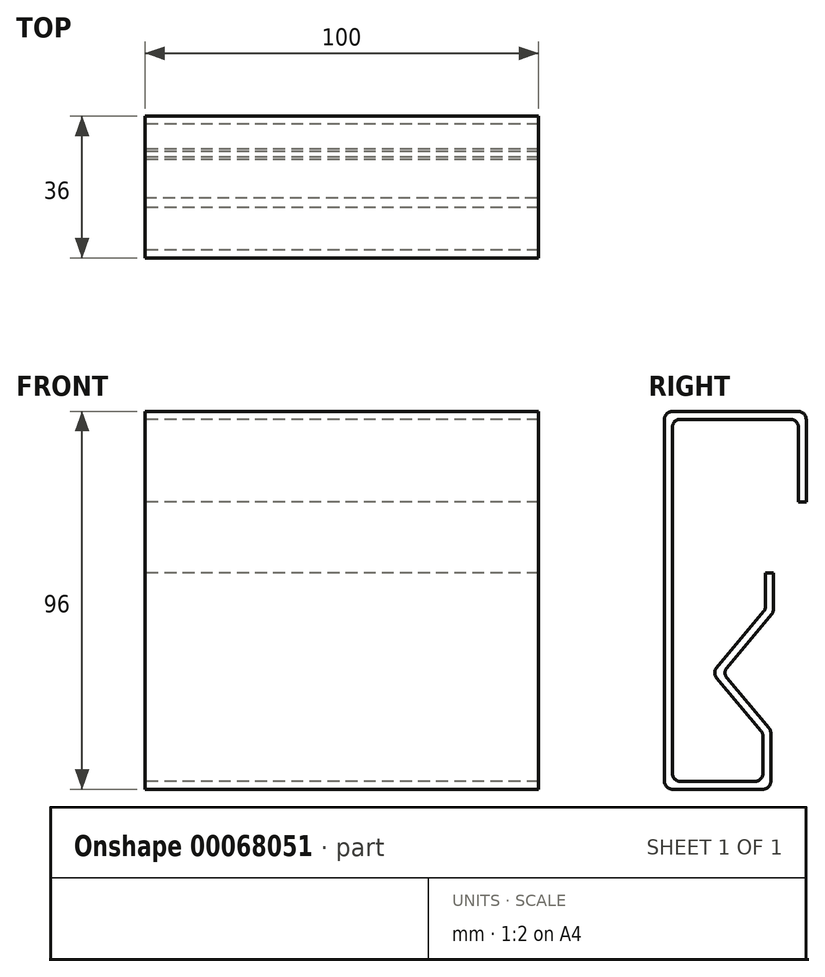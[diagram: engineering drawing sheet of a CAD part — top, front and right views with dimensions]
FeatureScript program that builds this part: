
annotation { "Feature Type Name" : "Feature", "Feature Type Description" : "" }
export const myFeature = defineFeature(function(context is Context, id is Id, definition is map)
    precondition{}
    {
        {
            var Q0;
            Q0=qCreatedBy(makeId("Right.planeOp"),FACE);
            var sketch = newSketch(context, id + "F0", { "sketchPlane" : qUnion([Q0])});
            skLineSegment(sketch, "E0", {"start": v(36, -23) * mm, "end": v(36, 0) * mm});
            skLineSegment(sketch, "E1", {"start": v(36, 0) * mm, "end": v(0, 0) * mm});
            skLineSegment(sketch, "E2", {"start": v(0, 0) * mm, "end": v(0, -96) * mm});
            skLineSegment(sketch, "E3", {"start": v(0, -96) * mm, "end": v(27, -96) * mm});
            skLineSegment(sketch, "E4", {"start": v(34, -23) * mm, "end": v(36, -23) * mm});
            skLineSegment(sketch, "E5.1", {"start": v(2, -2) * mm, "end": v(2, -94) * mm});
            skLineSegment(sketch, "E5.2", {"start": v(34, -2) * mm, "end": v(2, -2) * mm});
            skLineSegment(sketch, "E5.3", {"start": v(34, -23) * mm, "end": v(34, -2) * mm});
            skLineSegment(sketch, "E6", {"start": v(27, -96) * mm, "end": v(27, -81) * mm});
            skLineSegment(sketch, "E7", {"start": v(27, -81) * mm, "end": v(14.76, -66.4) * mm});
            skLineSegment(sketch, "E8", {"start": v(14.76, -66.4) * mm, "end": v(27.64, -51.05) * mm});
            skLineSegment(sketch, "E9", {"start": v(27.64, -51.05) * mm, "end": v(27.64, -41.05) * mm});
            skLineSegment(sketch, "E10.0", {"start": v(25.64, -50.32) * mm, "end": v(25.64, -41.05) * mm});
            skLineSegment(sketch, "E10.1", {"start": v(2, -94) * mm, "end": v(25, -94) * mm});
            skLineSegment(sketch, "E10.2", {"start": v(25, -94) * mm, "end": v(25, -81.73) * mm});
            skLineSegment(sketch, "E10.3", {"start": v(25, -81.73) * mm, "end": v(12.14, -66.4) * mm});
            skLineSegment(sketch, "E10.4", {"start": v(12.14, -66.4) * mm, "end": v(25.64, -50.32) * mm});
            skLineSegment(sketch, "E11", {"start": v(27.64, -41.05) * mm, "end": v(25.64, -41.05) * mm});
            skSolve(sketch);
        }
        {
            var Q0;
            Q0=makeQuery(id+"F0.imprint","IMPRINT",FACE,{"disambiguationData":[TD([[makeQuery(id+"F0.imprint","IMPRINT",EDGE,{"derivedFrom":sQuery(id+"F0.wireOp",EDGE,"E0")}),1.0]])]});
            extrude(context, id + "F1", {"entities" : qUnion([Q0]), "depth" : 100 * mm});
        }
        {
            var Q0;
            Q0=makeQuery(id+"F1.opExtrude","SWEPT_EDGE",EDGE,{"disambiguationData":[OSD([sQuery(id+"F0.wireOp",EDGE,"E0"),sQuery(id+"F0.wireOp",EDGE,"E1")])]});
            var Q1;
            Q1=makeQuery(id+"F1.opExtrude","SWEPT_EDGE",EDGE,{"disambiguationData":[OSD([sQuery(id+"F0.wireOp",EDGE,"E1"),sQuery(id+"F0.wireOp",EDGE,"E2")])]});
            var Q2;
            Q2=makeQuery(id+"F1.opExtrude","SWEPT_EDGE",EDGE,{"disambiguationData":[OSD([sQuery(id+"F0.wireOp",EDGE,"E5.2"),sQuery(id+"F0.wireOp",EDGE,"E5.3")])]});
            var Q3;
            Q3=makeQuery(id+"F1.opExtrude","SWEPT_EDGE",EDGE,{"disambiguationData":[OSD([sQuery(id+"F0.wireOp",EDGE,"E5.1"),sQuery(id+"F0.wireOp",EDGE,"E5.2")])]});
            var Q4;
            Q4=makeQuery(id+"F1.opExtrude","SWEPT_EDGE",EDGE,{"disambiguationData":[OSD([sQuery(id+"F0.wireOp",EDGE,"E2"),sQuery(id+"F0.wireOp",EDGE,"E3")])]});
            var Q5;
            Q5=makeQuery(id+"F1.opExtrude","SWEPT_EDGE",EDGE,{"disambiguationData":[OSD([sQuery(id+"F0.wireOp",EDGE,"E3"),sQuery(id+"F0.wireOp",EDGE,"E6")])]});
            var Q6;
            Q6=makeQuery(id+"F1.opExtrude","SWEPT_EDGE",EDGE,{"disambiguationData":[OSD([sQuery(id+"F0.wireOp",EDGE,"E6"),sQuery(id+"F0.wireOp",EDGE,"E7")])]});
            var Q7;
            Q7=makeQuery(id+"F1.opExtrude","SWEPT_EDGE",EDGE,{"disambiguationData":[OSD([sQuery(id+"F0.wireOp",EDGE,"E7"),sQuery(id+"F0.wireOp",EDGE,"E8")])]});
            var Q8;
            Q8=makeQuery(id+"F1.opExtrude","SWEPT_EDGE",EDGE,{"disambiguationData":[OSD([sQuery(id+"F0.wireOp",EDGE,"E8"),sQuery(id+"F0.wireOp",EDGE,"E9")])]});
            var Q9;
            Q9=makeQuery(id+"F1.opExtrude","SWEPT_EDGE",EDGE,{"disambiguationData":[OSD([sQuery(id+"F0.wireOp",EDGE,"E5.1"),sQuery(id+"F0.wireOp",EDGE,"E10.1")])]});
            var Q10;
            Q10=makeQuery(id+"F1.opExtrude","SWEPT_EDGE",EDGE,{"disambiguationData":[OSD([sQuery(id+"F0.wireOp",EDGE,"E10.1"),sQuery(id+"F0.wireOp",EDGE,"E10.2")])]});
            var Q11;
            Q11=makeQuery(id+"F1.opExtrude","SWEPT_EDGE",EDGE,{"disambiguationData":[OSD([sQuery(id+"F0.wireOp",EDGE,"E10.2"),sQuery(id+"F0.wireOp",EDGE,"E10.3")])]});
            var Q12;
            Q12=makeQuery(id+"F1.opExtrude","SWEPT_EDGE",EDGE,{"disambiguationData":[OSD([sQuery(id+"F0.wireOp",EDGE,"E10.3"),sQuery(id+"F0.wireOp",EDGE,"E10.4")])]});
            var Q13;
            Q13=makeQuery(id+"F1.opExtrude","SWEPT_EDGE",EDGE,{"disambiguationData":[OSD([sQuery(id+"F0.wireOp",EDGE,"E10.0"),sQuery(id+"F0.wireOp",EDGE,"E10.4")])]});
            fillet(context, id + "F2", {"entities" : qUnion([Q0, Q1, Q2, Q3, Q4, Q5, Q6, Q7, Q8, Q9, Q10, Q11, Q12, Q13]), "radius" : 2 * mm, "tangentPropagation" : true, "allowEdgeOverflow" : false});
        }
    });
